# Revit family: Tub_Faucet-Freestanding-Grohe-Allure-25222_Series
name_source: partatom
category: Plumbing Fixtures
units: mm (PartAtom-declared; Revit-internal decimal feet)

## family parameters
Always vertical = No
Cut with Voids When Loaded = No
OmniClass Number = 23.45.55.17
OmniClass Title = Mixing Faucets
Part Type = Normal
Room Calculation Point = No
Round Connector Dimension = Use Diameter
Shared = Yes
Work Plane-Based = Yes

## types (4) — shared parameters
ASME A112.18.1/CSA B125.1 = Yes
Assembly Code = D2020300
CEC Compliant = Yes
CW Connection = No
CWFU = 3
CalGreen Compliant = Yes
Default Elevation = 0"
Description = Allure Single-Handle Freestanding Tub with Faucet 1.2 GPM Hand Shower
Flow Rate = 1.75 gpm
GROHE DreamSpray = Yes
GROHE EcoJoy = Yes
GROHE StarLight = Yes
HW Connection = No
HWFU = 3
IAPMO Compliance = • WaterSense • Low Lead Certified • Massachusetts Plumbing Board Approved • Energy Policy Act of 1992 • NSF 61• NSF 372 • Complies with lead plumbing laws
Installation Type = Surface Mounted
Length = 10 3/8"
Manufacturer = GROHE
Orifice Material = Rubber-Grohe-Grey
Plate Width = 6 11/16"
Price = Prices may vary. Please consult Manufacturer Representative for most up-to-date price list.
Rough-In Set (29 038 001) = No
Spout Height = 9 1/16"
Tempered Water Connection = Yes
Tempered Water Connection Diameter = 1/2"
Vent Connection = No
WFU = 4
Waste Connection = No
Width = 4"

## per-type parameters (varying)
| type | Finish | Height | Material | Nominal Height | Product Documentation Link | Product Page URL | URL |
| 25222001 | Metal-Grohe-001-StarLight Chrome | 34 9/16" | Metal-Grohe-001-StarLight Chrome | 66" | https://lixil.cdn.celum.cloud | https://www.grohe.us | https://www.grohe.com |
| 25222EN1 | Metal-Grohe-EN1-Brushed Nickel InfinityFinish | 30 1/2" | Metal-Grohe-EN1-Brushed Nickel InfinityFinish | 0" | https://lixil.cdn.celum.cloud | https://www.grohe.us | https://www.grohe.us |
| 25222GN1 | Metal-Grohe-GN1-Brushed Cool Sunrise | 30 1/2" | Metal-Grohe-GN1-Brushed Cool Sunrise | 0" |  |  | https://www.grohe.us |
| 252222431 | Metal-Grohe-2431-Matte Black | 30 1/2" | Metal-Grohe-2431-Matte Black | 0" |  |  | https://www.grohe.us |

note: column(s) folded — value = type name in every type: Model

## geometry (parser evidence)
native form markers: Sweep x4
no freeform markers — native parametric forms only
